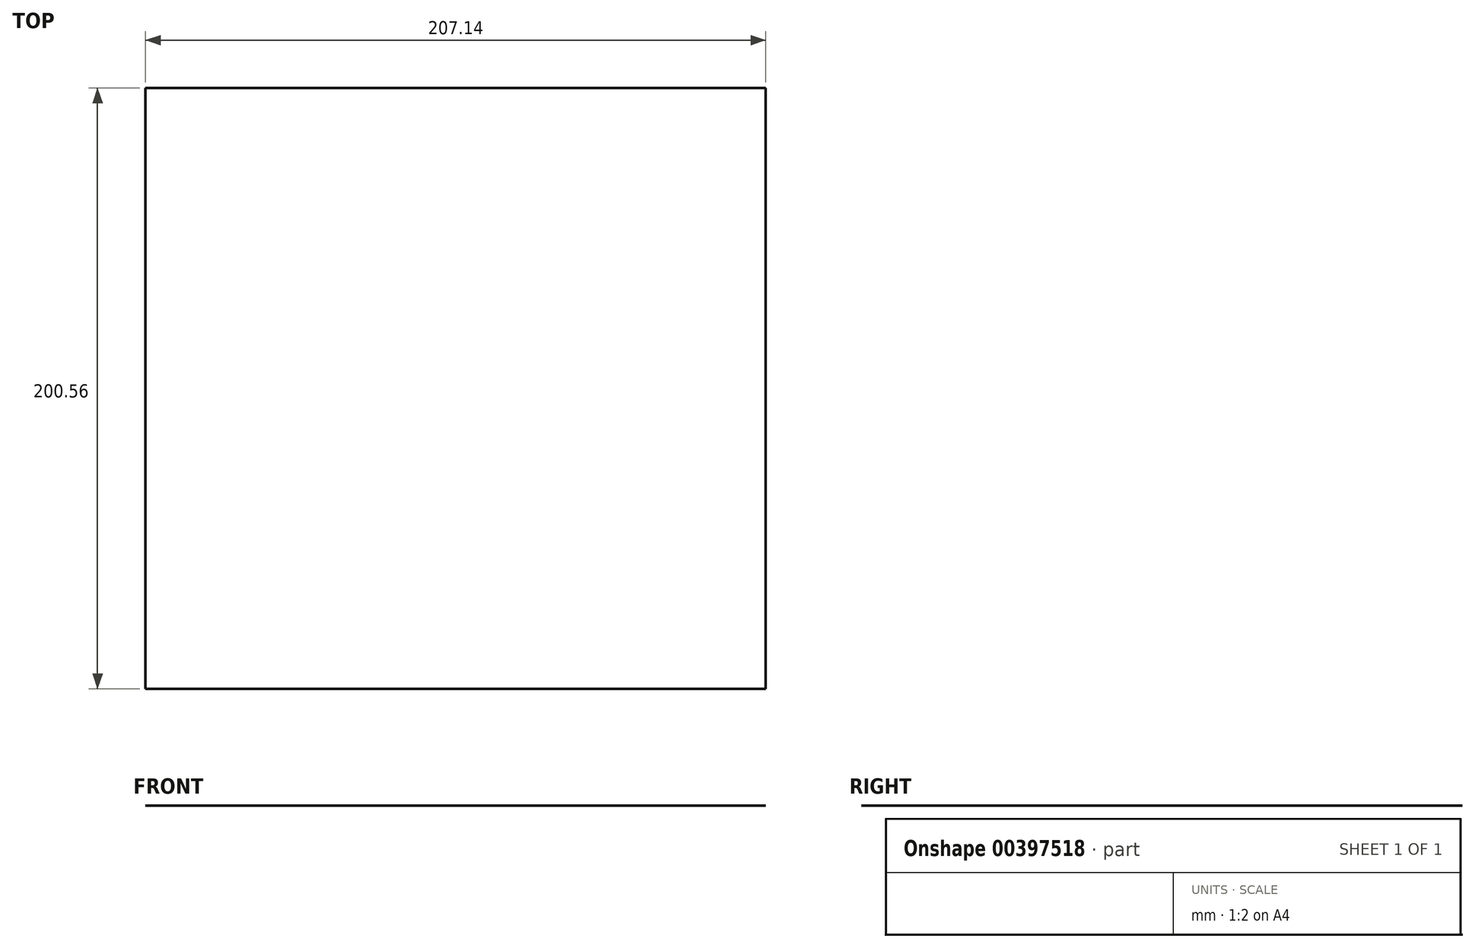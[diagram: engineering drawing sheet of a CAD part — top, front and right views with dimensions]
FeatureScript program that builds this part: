
annotation { "Feature Type Name" : "Feature", "Feature Type Description" : "" }
export const myFeature = defineFeature(function(context is Context, id is Id, definition is map)
    precondition{}
    {
        {
            var Q0;
            Q0=qCreatedBy(makeId("Top.planeOp"),FACE);
            var sketch = newSketch(context, id + "F0", { "sketchPlane" : qUnion([Q0])});
            skLineSegment(sketch, "E0.bottom", {"start": v(-103.57, -100.28) * mm, "end": v(103.57, -100.28) * mm});
            skLineSegment(sketch, "E0.top", {"start": v(-103.57, 100.28) * mm, "end": v(103.57, 100.28) * mm});
            skLineSegment(sketch, "E0.left", {"start": v(-103.57, -100.28) * mm, "end": v(-103.57, 100.28) * mm});
            skLineSegment(sketch, "E0.right", {"start": v(103.57, -100.28) * mm, "end": v(103.57, 100.28) * mm});
            skPoint(sketch, "E0.middle", {"position": v(0, 0) * mm});
            skSolve(sketch);
        }
        {
            var Q0;
            Q0 = qSketchRegion(id + "F0", true);
            extrude(context, id + "F1", {"entities" : qUnion([Q0]), "depth" : 1 / 203.2 * mm});
        }
    });
